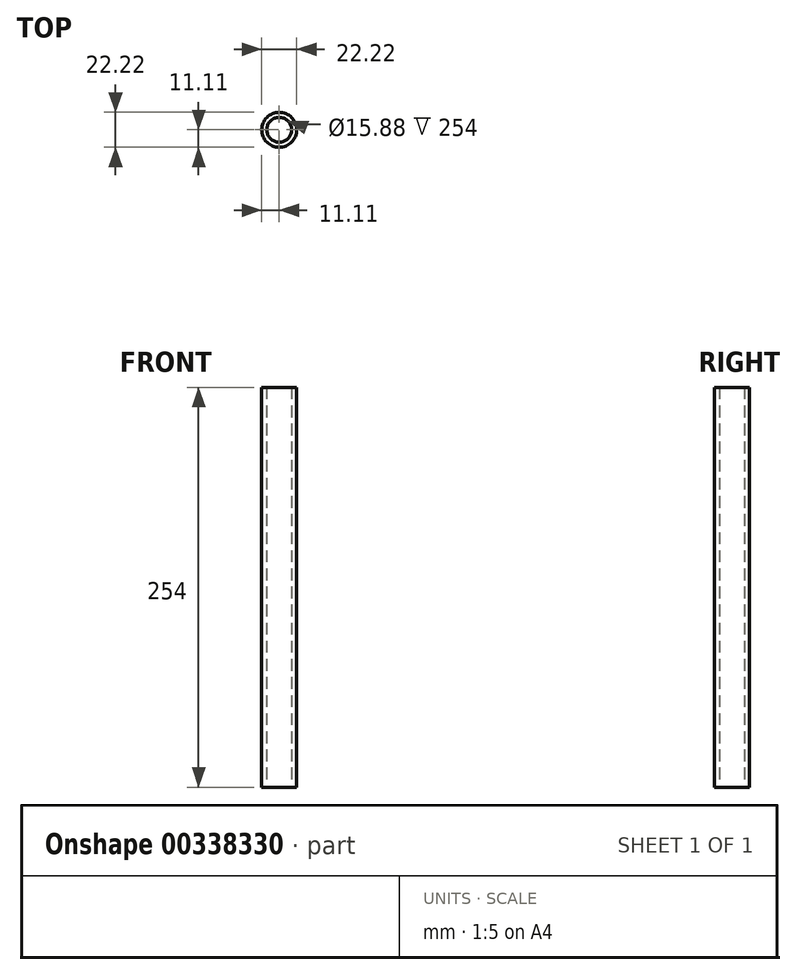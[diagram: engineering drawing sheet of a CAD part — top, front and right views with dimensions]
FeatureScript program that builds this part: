
annotation { "Feature Type Name" : "Feature", "Feature Type Description" : "" }
export const myFeature = defineFeature(function(context is Context, id is Id, definition is map)
    precondition{}
    {
        {
            var Q0;
            Q0=qCreatedBy(makeId("Top.planeOp"),FACE);
            var sketch = newSketch(context, id + "F0", { "sketchPlane" : qUnion([Q0])});
            skCircle(sketch, "E0", {"center": v(0, 0) * mm, "radius": 7.94 * mm});
            skCircle(sketch, "E1", {"center": v(0, 0) * mm, "radius": 11.11 * mm});
            skSolve(sketch);
        }
        {
            var Q0;
            Q0=qSketchRegion(id+"F0",true);
            extrude(context, id + "F1", {"entities" : qUnion([Q0]), "depth" : 254 * mm});
        }
    });
